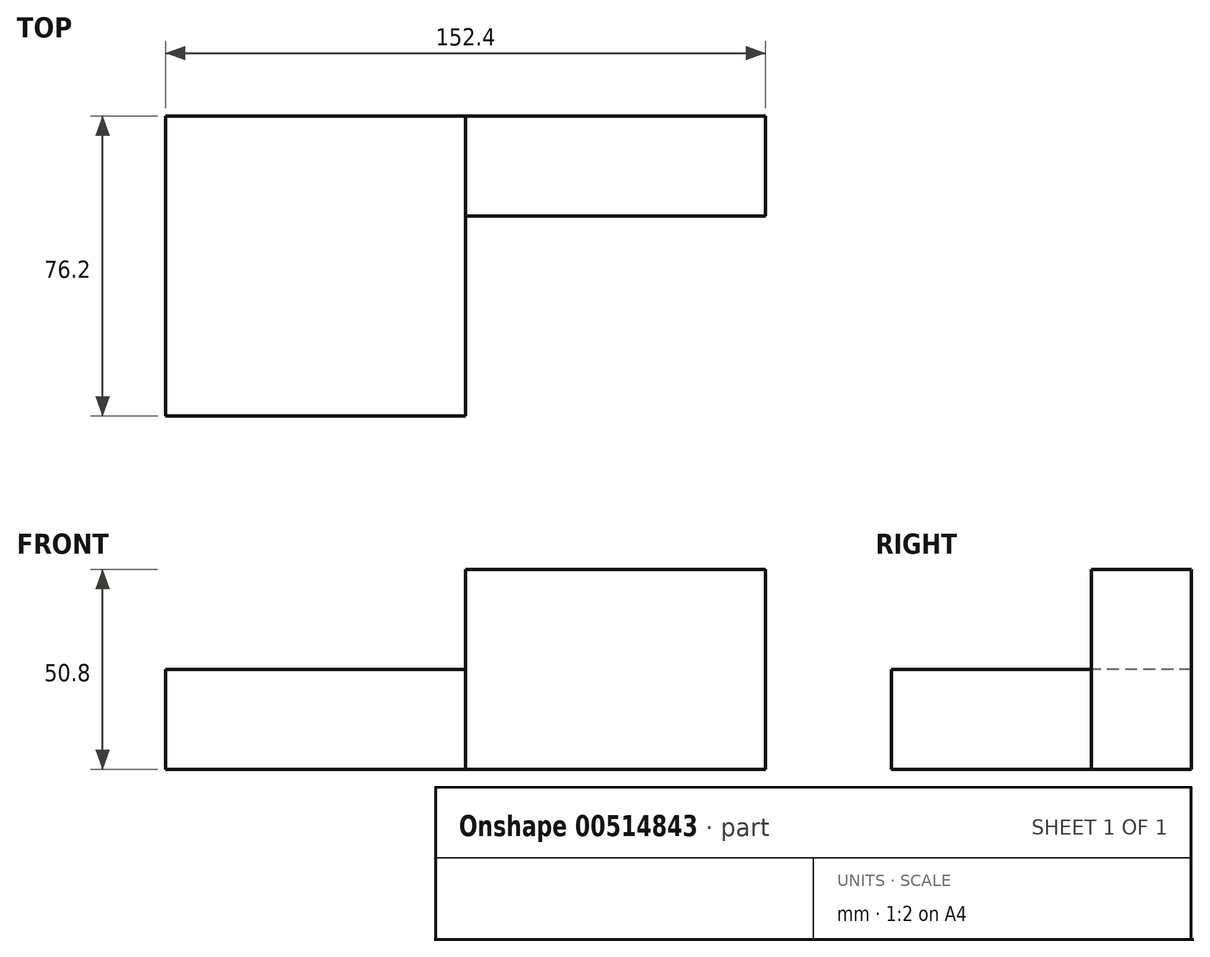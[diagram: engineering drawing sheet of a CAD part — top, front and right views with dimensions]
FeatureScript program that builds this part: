
annotation { "Feature Type Name" : "Feature", "Feature Type Description" : "" }
export const myFeature = defineFeature(function(context is Context, id is Id, definition is map)
    precondition{}
    {
        {
            var Q0;
            Q0=qCreatedBy(makeId("Top.planeOp"),FACE);
            var sketch = newSketch(context, id + "F0", { "sketchPlane" : qUnion([Q0])});
            skLineSegment(sketch, "E0.bottom", {"start": v(8.11, 109.2) * mm, "end": v(84.31, 109.2) * mm});
            skLineSegment(sketch, "E0.top", {"start": v(8.11, 83.8) * mm, "end": v(84.31, 83.8) * mm});
            skLineSegment(sketch, "E0.left", {"start": v(8.11, 109.2) * mm, "end": v(8.11, 83.8) * mm});
            skLineSegment(sketch, "E0.right", {"start": v(84.31, 109.2) * mm, "end": v(84.31, 83.8) * mm});
            skLineSegment(sketch, "E1.top", {"start": v(8.11, 58.4) * mm, "end": v(84.31, 58.4) * mm});
            skLineSegment(sketch, "E1.left", {"start": v(8.11, 83.8) * mm, "end": v(8.11, 58.4) * mm});
            skLineSegment(sketch, "E1.right", {"start": v(84.31, 83.8) * mm, "end": v(84.31, 58.4) * mm});
            skLineSegment(sketch, "E2.top", {"start": v(8.11, 33) * mm, "end": v(84.31, 33) * mm});
            skLineSegment(sketch, "E2.left", {"start": v(8.11, 58.4) * mm, "end": v(8.11, 33) * mm});
            skLineSegment(sketch, "E2.right", {"start": v(84.31, 58.4) * mm, "end": v(84.31, 33) * mm});
            skLineSegment(sketch, "E3.bottom", {"start": v(-68.09, 109.2) * mm, "end": v(8.11, 109.2) * mm});
            skLineSegment(sketch, "E3.top", {"start": v(-68.09, 33) * mm, "end": v(8.11, 33) * mm});
            skLineSegment(sketch, "E3.left", {"start": v(-68.09, 109.2) * mm, "end": v(-68.09, 33) * mm});
            skLineSegment(sketch, "E3.right", {"start": v(8.11, 109.2) * mm, "end": v(8.11, 33) * mm});
            skSolve(sketch);
        }
        {
            var Q0;
            {var subQ1=sQuery(id+"F0.wireOp",EDGE,"E3.bottom");Q0=makeQuery(id+"F0.imprint","IMPRINT",FACE,{"disambiguationData":[TD([[makeQuery(id+"F0.imprint","IMPRINT",EDGE,{"derivedFrom":subQ1}),-1.0]])]});}
            var Q1;
            {var subQ0=sQuery(id+"F0.wireOp",EDGE,"E0.top");Q1=makeQuery(id+"F0.imprint","IMPRINT",FACE,{"disambiguationData":[TD([[makeQuery(id+"F0.imprint","IMPRINT",EDGE,{"derivedFrom":subQ0}),-1.0]])]});}
            extrude(context, id + "F1", {"entities" : qUnion([Q0, Q1]), "depth" : 25.4 * mm, "offsetDistance" : 25.4 * mm});
        }
        {
            var Q0;
            {var subQ0=sQuery(id+"F0.wireOp",EDGE,"E0.bottom");Q0=makeQuery(id+"F0.imprint","IMPRINT",FACE,{"disambiguationData":[TD([[makeQuery(id+"F0.imprint","IMPRINT",EDGE,{"derivedFrom":subQ0}),-1.0]])]});}
            var Q1;
            {var subQ0=sQuery(id+"F0.wireOp",EDGE,"E1.top");Q1=makeQuery(id+"F0.imprint","IMPRINT",FACE,{"disambiguationData":[TD([[makeQuery(id+"F0.imprint","IMPRINT",EDGE,{"derivedFrom":subQ0}),-1.0]])]});}
            extrude(context, id + "F2", {"entities" : qUnion([Q0, Q1]), "operationType" : NewBodyOperationType.ADD, "depth" : 50.8 * mm, "offsetDistance" : 25.4 * mm});
        }
    });
